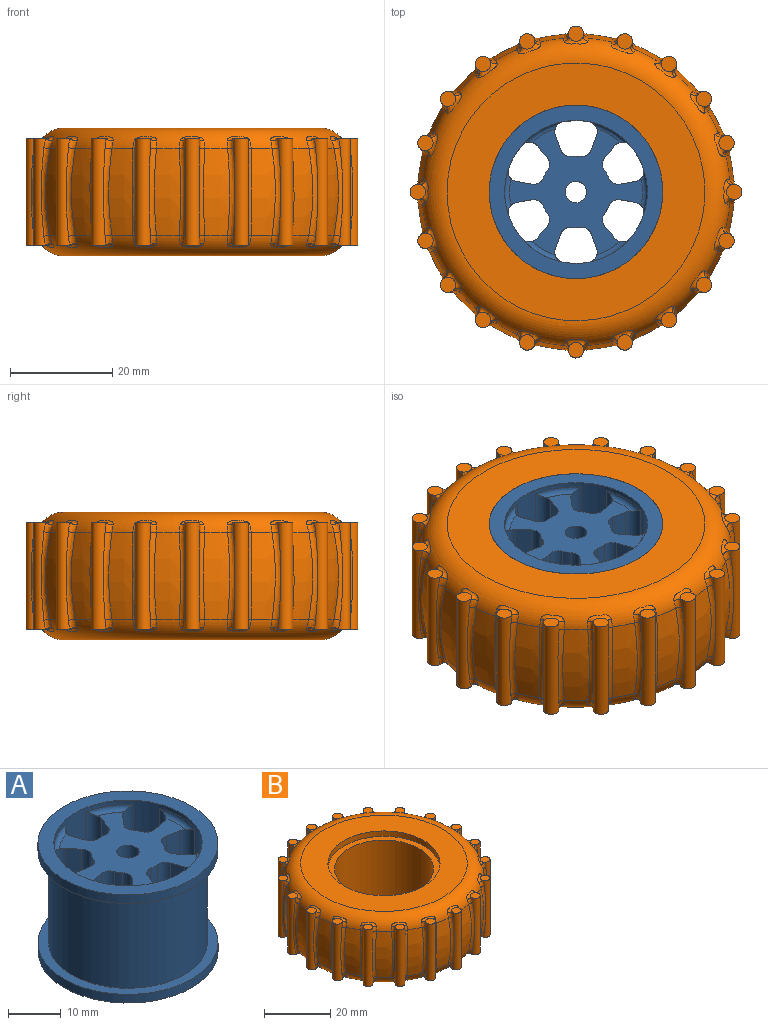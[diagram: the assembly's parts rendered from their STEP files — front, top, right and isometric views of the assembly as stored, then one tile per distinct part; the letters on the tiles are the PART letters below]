
ASSEMBLY  parts=2 mates=1
PART A: 60 faces, bbox 34x34x25 mm
  f0: cylinder r=15mm len=30mm, axis (0,0,-1), area 1979.2mm2, adj f19,f21
  f1: plane 16.45x3.01mm, normal (-0.17,0.98,0), area 49.3mm2, adj f3,f4,f13,f16
  f2: plane 16.45x2.34mm, normal (0.77,-0.64,0), area 49.3mm2, adj f5,f6,f13,f17
  f3: cylinder r=2mm len=20.5mm, axis (0,0,-1), area 62.2mm2, adj f1,f10,f13,f15,f16
  f4: cylinder r=2mm len=19.5mm, axis (0,0,-1), area 47.8mm2, adj f1,f8,f13,f16
  f5: cylinder r=2mm len=19.5mm, axis (0,0,-1), area 47.8mm2, adj f2,f8,f13,f17
  f6: cylinder r=2mm len=20.5mm, axis (0,0,-1), area 62.2mm2, adj f2,f10,f13,f14,f17
  f7: plane 34x34mm, normal (0,0,-1), area 292.2mm2, adj f10,f20
  f8: cylinder r=7mm len=23mm, axis (0,0,-1), area 358.6mm2, adj f4,f5,f12,f13,f16,f17,f25,f26
  f9: cylinder r=2.1mm len=23mm, axis (0,0,-1), area 303.5mm2, adj f12,f13
  f10: cylinder r=14mm len=28mm, axis (0,0,-1), area 1021.3mm2, adj f3,f6,f7,f11,f14,f15,f16,f17
  f11: plane 34x34mm, normal (0,0,1), area 292.2mm2, adj f10,f18
  f12: plane 14x14mm, normal (0,0,-1), area 140.1mm2, adj f8,f9
  f13: plane 26x24.68mm, normal (0,0,1), area 274.5mm2, adj f1,f2,f3,f4,f5,f6,f8,f9
  f14: torus R=13mm, axis (0,0,1), area 11.4mm2, adj f6,f10,f13,f24
  f15: torus R=13mm, axis (0,0,1), area 11.4mm2, adj f3,f10,f13,f59
  f16: torus R=10.5mm, axis (0,0,-1), area 52mm2, adj f1,f3,f4,f8,f10,f55,f58,f59
  f17: torus R=10.5mm, axis (0,0,-1), area 52mm2, adj f2,f5,f6,f8,f10,f22,f24,f25
  f18: cylinder r=17mm len=34mm, axis (0,0,1), area 213.6mm2, adj f11,f19
  f19: plane 34x34mm, normal (0,0,-1), area 201.1mm2, adj f0,f18
  f20: cylinder r=17mm len=34mm, axis (0,0,-1), area 213.6mm2, adj f7,f21
  f21: plane 34x34mm, normal (0,0,1), area 201.1mm2, adj f0,f20
  f22: plane 16.45x2.87mm, normal (-0.94,0.34,0), area 49.3mm2, adj f13,f17,f24,f25
  f23: plane 16.45x2.87mm, normal (0.94,0.34,0), area 49.3mm2, adj f13,f26,f27,f29
  f24: cylinder r=2mm len=20.5mm, axis (0,0,-1), area 62.2mm2, adj f10,f13,f14,f17,f22
  f25: cylinder r=2mm len=19.5mm, axis (0,0,-1), area 47.8mm2, adj f8,f13,f17,f22
  f26: cylinder r=2mm len=19.5mm, axis (0,0,-1), area 47.8mm2, adj f8,f13,f23,f29
  f27: cylinder r=2mm len=20.5mm, axis (0,0,-1), area 62.2mm2, adj f10,f13,f23,f28,f29
  f28: torus R=13mm, axis (0,0,1), area 11.4mm2, adj f10,f13,f27,f32
  f29: torus R=10.5mm, axis (0,0,-1), area 52mm2, adj f8,f10,f23,f26,f27,f30,f32,f33
  f30: plane 16.45x2.34mm, normal (-0.77,-0.64,0), area 49.3mm2, adj f13,f29,f32,f33
  f31: plane 16.45x3.01mm, normal (0.17,0.98,0), area 49.3mm2, adj f13,f34,f35,f37
  f32: cylinder r=2mm len=20.5mm, axis (0,0,-1), area 62.2mm2, adj f10,f13,f28,f29,f30
  f33: cylinder r=2mm len=19.5mm, axis (0,0,-1), area 47.8mm2, adj f8,f13,f29,f30
  f34: cylinder r=2mm len=19.5mm, axis (0,0,-1), area 47.8mm2, adj f8,f13,f31,f37
  f35: cylinder r=2mm len=20.5mm, axis (0,0,-1), area 62.2mm2, adj f10,f13,f31,f36,f37
  f36: torus R=13mm, axis (0,0,1), area 11.4mm2, adj f10,f13,f35,f40
  f37: torus R=10.5mm, axis (0,0,-1), area 52mm2, adj f8,f10,f31,f34,f35,f38,f40,f41
  f38: plane 16.45x3.01mm, normal (0.17,-0.98,0), area 49.3mm2, adj f13,f37,f40,f41
  f39: plane 16.45x2.34mm, normal (-0.77,0.64,0), area 49.3mm2, adj f13,f42,f43,f45
  f40: cylinder r=2mm len=20.5mm, axis (0,0,-1), area 62.2mm2, adj f10,f13,f36,f37,f38
  f41: cylinder r=2mm len=19.5mm, axis (0,0,-1), area 47.8mm2, adj f8,f13,f37,f38
  f42: cylinder r=2mm len=19.5mm, axis (0,0,-1), area 47.8mm2, adj f8,f13,f39,f45
  f43: cylinder r=2mm len=20.5mm, axis (0,0,-1), area 62.2mm2, adj f10,f13,f39,f44,f45
  f44: torus R=13mm, axis (0,0,1), area 11.4mm2, adj f10,f13,f43,f48
  f45: torus R=10.5mm, axis (0,0,-1), area 52mm2, adj f8,f10,f39,f42,f43,f46,f48,f49
  f46: plane 16.45x2.87mm, normal (0.94,-0.34,0), area 49.3mm2, adj f13,f45,f48,f49
  f47: plane 16.45x2.87mm, normal (-0.94,-0.34,0), area 49.3mm2, adj f13,f50,f51,f53
  f48: cylinder r=2mm len=20.5mm, axis (0,0,-1), area 62.2mm2, adj f10,f13,f44,f45,f46
  f49: cylinder r=2mm len=19.5mm, axis (0,0,-1), area 47.8mm2, adj f8,f13,f45,f46
  f50: cylinder r=2mm len=19.5mm, axis (0,0,-1), area 47.8mm2, adj f8,f13,f47,f53
  f51: cylinder r=2mm len=20.5mm, axis (0,0,-1), area 62.2mm2, adj f10,f13,f47,f52,f53
  f52: torus R=13mm, axis (0,0,1), area 11.4mm2, adj f10,f13,f51,f56
  f53: torus R=10.5mm, axis (0,0,-1), area 52mm2, adj f8,f10,f47,f50,f51,f54,f56,f57
  f54: plane 16.45x2.34mm, normal (0.77,0.64,0), area 49.3mm2, adj f13,f53,f56,f57
  f55: plane 16.45x3.01mm, normal (-0.17,-0.98,0), area 49.3mm2, adj f13,f16,f58,f59
  f56: cylinder r=2mm len=20.5mm, axis (0,0,-1), area 62.2mm2, adj f10,f13,f52,f53,f54
  f57: cylinder r=2mm len=19.5mm, axis (0,0,-1), area 47.8mm2, adj f8,f13,f53,f54
  f58: cylinder r=2mm len=19.5mm, axis (0,0,-1), area 47.8mm2, adj f8,f13,f16,f55
  f59: cylinder r=2mm len=20.5mm, axis (0,0,-1), area 62.2mm2, adj f10,f13,f15,f16,f55
PART B: 277 faces, bbox 65.5x65.5x25 mm
  f0: torus R=25.25mm, axis (0,0,-1), area 977.2mm2, adj f1,f2,f3,f4,f5,f6,f7,f8
  f1: revolved ~16.97x4.97mm, area 85.1mm2, adj f0,f21,f47,f246
  f2: revolved ~16.97x5.22mm, area 85.1mm2, adj f0,f21,f37,f243
  f3: revolved ~16.97x5.22mm, area 85.1mm2, adj f0,f21,f34,f234
  f4: revolved ~16.97x4.97mm, area 85.1mm2, adj f0,f21,f223,f233
  f5: revolved ~16.97x4.24mm, area 85.1mm2, adj f0,f21,f212,f222
  f6: revolved ~16.97x4.97mm, area 85.1mm2, adj f0,f21,f201,f211
  f7: revolved ~16.97x5.22mm, area 85.1mm2, adj f0,f21,f190,f200
  f8: revolved ~16.97x5.22mm, area 85.1mm2, adj f0,f21,f179,f189
  f9: revolved ~16.97x4.97mm, area 85.1mm2, adj f0,f21,f168,f178
  f10: revolved ~16.97x4.24mm, area 85.1mm2, adj f0,f21,f157,f167
  f11: revolved ~16.97x4.97mm, area 85.1mm2, adj f0,f21,f146,f156
  f12: revolved ~16.97x5.22mm, area 85.1mm2, adj f0,f21,f135,f145
  f13: revolved ~16.97x5.22mm, area 85.1mm2, adj f0,f21,f124,f134
  f14: revolved ~16.97x4.97mm, area 85.1mm2, adj f0,f21,f113,f123
  f15: revolved ~16.97x4.24mm, area 85.1mm2, adj f0,f21,f102,f112
  f16: revolved ~16.97x4.97mm, area 85.1mm2, adj f0,f21,f91,f101
  f17: revolved ~16.97x5.22mm, area 85.1mm2, adj f0,f21,f80,f90
  f18: revolved ~16.97x5.22mm, area 85.1mm2, adj f0,f21,f69,f79
  f19: revolved ~16.97x4.97mm, area 85.1mm2, adj f0,f21,f58,f68
  f20: revolved ~16.97x4.24mm, area 85.1mm2, adj f0,f21,f46,f57
  f21: torus R=25.25mm, axis (0,0,-1), area 977.2mm2, adj f1,f2,f3,f4,f5,f6,f7,f8
  f22: plane 34x34mm, normal (0,0,1), area 201.1mm2, adj f23,f28
  f23: cylinder r=15mm len=30mm, axis (0,0,-1), area 1979.2mm2, adj f22,f24
  f24: plane 34x34mm, normal (0,0,-1), area 201.1mm2, adj f23,f25
  f25: cylinder r=17mm len=34mm, axis (0,0,-1), area 213.6mm2, adj f24,f26
  f26: plane 50.51x50.51mm, normal (0,0,-1), area 1095.4mm2, adj f0,f25
  f27: plane 50.51x50.51mm, normal (0,0,1), area 1095.4mm2, adj f21,f28
  f28: cylinder r=17mm len=34mm, axis (0,0,-1), area 213.6mm2, adj f22,f27
  f29: cylinder r=1.5mm len=21mm, axis (0,0,1), area 87.2mm2, adj f30,f31,f32,f34,f35,f36,f37,f39
  f30: plane 3x3mm, normal (0,0,-1), area 7.1mm2, adj f29,f38
  f31: plane 3x3mm, normal (0,0,1), area 7.1mm2, adj f29,f33
  f32: bspline ~3.55x1.81mm, area 2.7mm2, adj f21,f29,f33,f34
  f33: bspline ~4.71x1.7mm, area 4.2mm2, adj f21,f31,f32,f35
  f34: bspline ~20.64x1.85mm, area 21.4mm2, adj f3,f29,f32,f36
  f35: bspline ~2.49x1.66mm, area 2.7mm2, adj f21,f29,f33,f37
  f36: bspline ~2.49x1.66mm, area 2.7mm2, adj f0,f29,f34,f38
  f37: bspline ~20.64x1.85mm, area 21.4mm2, adj f2,f29,f35,f39
  f38: bspline ~4.71x1.7mm, area 4.2mm2, adj f0,f30,f36,f39
  f39: bspline ~2.69x1.78mm, area 2.7mm2, adj f0,f29,f37,f38
  f40: plane 3x3mm, normal (0,0,-1), area 7.1mm2, adj f42,f49
  f41: plane 3x3mm, normal (0,0,1), area 7.1mm2, adj f42,f44
  f42: cylinder r=1.5mm len=21mm, axis (0,0,1), area 87.2mm2, adj f40,f41,f43,f45,f46,f47,f48,f50
  f43: bspline ~3.55x1.69mm, area 2.7mm2, adj f21,f42,f44,f47
  f44: bspline ~3.89x3.26mm, area 4.3mm2, adj f21,f41,f43,f45
  f45: bspline ~2.49x1.83mm, area 2.7mm2, adj f21,f42,f44,f46
  f46: bspline ~20.64x2.09mm, area 21.4mm2, adj f20,f42,f45,f48
  f47: bspline ~20.64x1.9mm, area 21.4mm2, adj f1,f42,f43,f50
  f48: bspline ~3.55x1.92mm, area 2.7mm2, adj f0,f42,f46,f49
  f49: bspline ~3.86x3.32mm, area 4.3mm2, adj f0,f40,f48,f50
  f50: bspline ~2.49x1.64mm, area 2.7mm2, adj f0,f42,f47,f49
  f51: plane 3x3mm, normal (0,0,-1), area 7.1mm2, adj f53,f60
  f52: plane 3x3mm, normal (0,0,1), area 7.1mm2, adj f53,f55
  f53: cylinder r=1.5mm len=21mm, axis (0,0,1), area 87.2mm2, adj f51,f52,f54,f56,f57,f58,f59,f61
  f54: bspline ~3.55x1.92mm, area 2.7mm2, adj f21,f53,f55,f57
  f55: bspline ~3.86x3.32mm, area 4.3mm2, adj f21,f52,f54,f56
  f56: bspline ~2.49x1.64mm, area 2.7mm2, adj f21,f53,f55,f58
  f57: bspline ~20.64x2.09mm, area 21.4mm2, adj f20,f53,f54,f61
  f58: bspline ~20.64x1.9mm, area 21.4mm2, adj f19,f53,f56,f59
  f59: bspline ~2.69x1.67mm, area 2.7mm2, adj f0,f53,f58,f60
  f60: bspline ~3.89x3.26mm, area 4.3mm2, adj f0,f51,f59,f61
  f61: bspline ~2.49x1.83mm, area 2.7mm2, adj f0,f53,f57,f60
  f62: plane 3x3mm, normal (0,0,-1), area 7.1mm2, adj f64,f71
  f63: plane 3x3mm, normal (0,0,1), area 7.1mm2, adj f64,f66
  f64: cylinder r=1.5mm len=21mm, axis (0,0,1), area 87.2mm2, adj f62,f63,f65,f67,f68,f69,f70,f72
  f65: bspline ~3.55x1.96mm, area 2.7mm2, adj f21,f64,f66,f68
  f66: bspline ~4.5x2.55mm, area 4.2mm2, adj f21,f63,f65,f67
  f67: bspline ~3.35x1.56mm, area 2.7mm2, adj f21,f64,f66,f69
  f68: bspline ~20.64x2.07mm, area 21.4mm2, adj f19,f64,f65,f72
  f69: bspline ~20.64x1.68mm, area 21.4mm2, adj f18,f64,f67,f70
  f70: bspline ~3.55x1.66mm, area 2.7mm2, adj f0,f64,f69,f71
  f71: bspline ~4.5x2.5mm, area 4.2mm2, adj f0,f62,f70,f72
  f72: bspline ~2.49x1.84mm, area 2.7mm2, adj f0,f64,f68,f71
  f73: plane 3x3mm, normal (0,0,-1), area 7.1mm2, adj f75,f82
  f74: plane 3x3mm, normal (0,0,1), area 7.1mm2, adj f75,f77
  f75: cylinder r=1.5mm len=21mm, axis (0,0,1), area 87.2mm2, adj f73,f74,f76,f78,f79,f80,f81,f83
  f76: bspline ~3.55x1.81mm, area 2.7mm2, adj f21,f75,f77,f79
  f77: bspline ~4.71x1.7mm, area 4.2mm2, adj f21,f74,f76,f78
  f78: bspline ~2.49x1.66mm, area 2.7mm2, adj f21,f75,f77,f80
  f79: bspline ~20.64x1.85mm, area 21.4mm2, adj f18,f75,f76,f83
  f80: bspline ~20.64x1.85mm, area 21.4mm2, adj f17,f75,f78,f81
  f81: bspline ~2.69x1.78mm, area 2.7mm2, adj f0,f75,f80,f82
  f82: bspline ~4.71x1.7mm, area 4.2mm2, adj f0,f73,f81,f83
  f83: bspline ~2.49x1.66mm, area 2.7mm2, adj f0,f75,f79,f82
  f84: plane 3x3mm, normal (0,0,-1), area 7.1mm2, adj f86,f93
  f85: plane 3x3mm, normal (0,0,1), area 7.1mm2, adj f86,f88
  f86: cylinder r=1.5mm len=21mm, axis (0,0,1), area 87.2mm2, adj f84,f85,f87,f89,f90,f91,f92,f94
  f87: bspline ~2.69x1.63mm, area 2.7mm2, adj f21,f86,f88,f90
  f88: bspline ~4.5x2.5mm, area 4.2mm2, adj f21,f85,f87,f89
  f89: bspline ~3.35x1.87mm, area 2.7mm2, adj f21,f86,f88,f91
  f90: bspline ~20.64x1.68mm, area 21.4mm2, adj f17,f86,f87,f94
  f91: bspline ~20.64x2.07mm, area 21.4mm2, adj f16,f86,f89,f92
  f92: bspline ~2.69x1.93mm, area 2.7mm2, adj f0,f86,f91,f93
  f93: bspline ~4.5x2.55mm, area 4.2mm2, adj f0,f84,f92,f94
  f94: bspline ~3.35x1.56mm, area 2.7mm2, adj f0,f86,f90,f93
  f95: plane 3x3mm, normal (0,0,-1), area 7.1mm2, adj f97,f104
  f96: plane 3x3mm, normal (0,0,1), area 7.1mm2, adj f97,f99
  f97: cylinder r=1.5mm len=21mm, axis (0,0,1), area 87.2mm2, adj f95,f96,f98,f100,f101,f102,f103,f105
  f98: bspline ~3.55x1.69mm, area 2.7mm2, adj f21,f97,f99,f101
  f99: bspline ~3.89x3.26mm, area 4.3mm2, adj f21,f96,f98,f100
  f100: bspline ~2.49x1.83mm, area 2.7mm2, adj f21,f97,f99,f102
  f101: bspline ~20.64x1.9mm, area 21.4mm2, adj f16,f97,f98,f105
  f102: bspline ~20.64x2.09mm, area 21.4mm2, adj f15,f97,f100,f103
  f103: bspline ~3.55x1.92mm, area 2.7mm2, adj f0,f97,f102,f104
  f104: bspline ~3.86x3.32mm, area 4.3mm2, adj f0,f95,f103,f105
  f105: bspline ~3.35x1.66mm, area 2.7mm2, adj f0,f97,f101,f104
  f106: plane 3x3mm, normal (0,0,-1), area 7.1mm2, adj f108,f115
  f107: plane 3x3mm, normal (0,0,1), area 7.1mm2, adj f108,f110
  f108: cylinder r=1.5mm len=21mm, axis (0,0,1), area 87.2mm2, adj f106,f107,f109,f111,f112,f113,f114,f116
  f109: bspline ~3.55x1.92mm, area 2.7mm2, adj f21,f108,f110,f112
  f110: bspline ~3.86x3.32mm, area 4.3mm2, adj f21,f107,f109,f111
  f111: bspline ~2.49x1.64mm, area 2.7mm2, adj f21,f108,f110,f113
  f112: bspline ~20.64x2.09mm, area 21.4mm2, adj f15,f108,f109,f116
  f113: bspline ~20.64x1.9mm, area 21.4mm2, adj f14,f108,f111,f114
  f114: bspline ~2.69x1.67mm, area 2.7mm2, adj f0,f108,f113,f115
  f115: bspline ~3.89x3.26mm, area 4.3mm2, adj f0,f106,f114,f116
  f116: bspline ~2.49x1.83mm, area 2.7mm2, adj f0,f108,f112,f115
  f117: plane 3x3mm, normal (0,0,-1), area 7.1mm2, adj f119,f126
  f118: plane 3x3mm, normal (0,0,1), area 7.1mm2, adj f119,f121
  f119: cylinder r=1.5mm len=21mm, axis (0,0,1), area 87.2mm2, adj f117,f118,f120,f122,f123,f124,f125,f127
  f120: bspline ~3.55x1.96mm, area 2.7mm2, adj f21,f119,f121,f123
  f121: bspline ~4.5x2.55mm, area 4.2mm2, adj f21,f118,f120,f122
  f122: bspline ~3.35x1.56mm, area 2.7mm2, adj f21,f119,f121,f124
  f123: bspline ~20.64x2.07mm, area 21.4mm2, adj f14,f119,f120,f127
  f124: bspline ~20.64x1.68mm, area 21.4mm2, adj f13,f119,f122,f125
  f125: bspline ~3.55x1.66mm, area 2.7mm2, adj f0,f119,f124,f126
  f126: bspline ~4.5x2.5mm, area 4.2mm2, adj f0,f117,f125,f127
  f127: bspline ~2.49x1.84mm, area 2.7mm2, adj f0,f119,f123,f126
  f128: plane 3x3mm, normal (0,0,-1), area 7.1mm2, adj f130,f137
  f129: plane 3x3mm, normal (0,0,1), area 7.1mm2, adj f130,f132
  f130: cylinder r=1.5mm len=21mm, axis (0,0,1), area 87.2mm2, adj f128,f129,f131,f133,f134,f135,f136,f138
  f131: bspline ~3.55x1.81mm, area 2.7mm2, adj f21,f130,f132,f134
  f132: bspline ~4.71x1.7mm, area 4.2mm2, adj f21,f129,f131,f133
  f133: bspline ~2.49x1.66mm, area 2.7mm2, adj f21,f130,f132,f135
  f134: bspline ~20.64x1.85mm, area 21.4mm2, adj f13,f130,f131,f138
  f135: bspline ~20.64x1.85mm, area 21.4mm2, adj f12,f130,f133,f136
  f136: bspline ~2.69x1.78mm, area 2.7mm2, adj f0,f130,f135,f137
  f137: bspline ~4.71x1.7mm, area 4.2mm2, adj f0,f128,f136,f138
  f138: bspline ~2.49x1.66mm, area 2.7mm2, adj f0,f130,f134,f137
  f139: plane 3x3mm, normal (0,0,-1), area 7.1mm2, adj f141,f148
  f140: plane 3x3mm, normal (0,0,1), area 7.1mm2, adj f141,f143
  f141: cylinder r=1.5mm len=21mm, axis (0,0,1), area 87.2mm2, adj f139,f140,f142,f144,f145,f146,f147,f149
  f142: bspline ~2.69x1.63mm, area 2.7mm2, adj f21,f141,f143,f145
  f143: bspline ~4.5x2.5mm, area 4.2mm2, adj f21,f140,f142,f144
  f144: bspline ~3.35x1.87mm, area 2.7mm2, adj f21,f141,f143,f146
  f145: bspline ~20.64x1.68mm, area 21.4mm2, adj f12,f141,f142,f149
  f146: bspline ~20.64x2.07mm, area 21.4mm2, adj f11,f141,f144,f147
  f147: bspline ~2.69x1.93mm, area 2.7mm2, adj f0,f141,f146,f148
  f148: bspline ~4.5x2.55mm, area 4.2mm2, adj f0,f139,f147,f149
  f149: bspline ~3.35x1.56mm, area 2.7mm2, adj f0,f141,f145,f148
  f150: plane 3x3mm, normal (0,0,-1), area 7.1mm2, adj f152,f159
  f151: plane 3x3mm, normal (0,0,1), area 7.1mm2, adj f152,f154
  f152: cylinder r=1.5mm len=21mm, axis (0,0,1), area 87.2mm2, adj f150,f151,f153,f155,f156,f157,f158,f160
  f153: bspline ~3.55x1.69mm, area 2.7mm2, adj f21,f152,f154,f156
  f154: bspline ~3.89x3.26mm, area 4.3mm2, adj f21,f151,f153,f155
  f155: bspline ~2.49x1.83mm, area 2.7mm2, adj f21,f152,f154,f157
  f156: bspline ~20.64x1.9mm, area 21.4mm2, adj f11,f152,f153,f160
  f157: bspline ~20.64x2.09mm, area 21.4mm2, adj f10,f152,f155,f158
  f158: bspline ~3.55x1.92mm, area 2.7mm2, adj f0,f152,f157,f159
  f159: bspline ~3.86x3.32mm, area 4.3mm2, adj f0,f150,f158,f160
  f160: bspline ~3.35x1.66mm, area 2.7mm2, adj f0,f152,f156,f159
  f161: plane 3x3mm, normal (0,0,-1), area 7.1mm2, adj f163,f170
  f162: plane 3x3mm, normal (0,0,1), area 7.1mm2, adj f163,f165
  f163: cylinder r=1.5mm len=21mm, axis (0,0,1), area 87.2mm2, adj f161,f162,f164,f166,f167,f168,f169,f171
  f164: bspline ~3.55x1.92mm, area 2.7mm2, adj f21,f163,f165,f167
  f165: bspline ~3.86x3.32mm, area 4.3mm2, adj f21,f162,f164,f166
  f166: bspline ~3.35x1.66mm, area 2.7mm2, adj f21,f163,f165,f168
  f167: bspline ~20.64x2.09mm, area 21.4mm2, adj f10,f163,f164,f171
  f168: bspline ~20.64x1.9mm, area 21.4mm2, adj f9,f163,f166,f169
  f169: bspline ~2.69x1.67mm, area 2.7mm2, adj f0,f163,f168,f170
  f170: bspline ~3.89x3.26mm, area 4.3mm2, adj f0,f161,f169,f171
  f171: bspline ~2.49x1.83mm, area 2.7mm2, adj f0,f163,f167,f170
  f172: plane 3x3mm, normal (0,0,-1), area 7.1mm2, adj f174,f181
  f173: plane 3x3mm, normal (0,0,1), area 7.1mm2, adj f174,f176
  f174: cylinder r=1.5mm len=21mm, axis (0,0,1), area 87.2mm2, adj f172,f173,f175,f177,f178,f179,f180,f182
  f175: bspline ~3.55x1.96mm, area 2.7mm2, adj f21,f174,f176,f178
  f176: bspline ~4.5x2.55mm, area 4.2mm2, adj f21,f173,f175,f177
  f177: bspline ~3.35x1.56mm, area 2.7mm2, adj f21,f174,f176,f179
  f178: bspline ~20.64x2.07mm, area 21.4mm2, adj f9,f174,f175,f182
  f179: bspline ~20.64x1.68mm, area 21.4mm2, adj f8,f174,f177,f180
  f180: bspline ~3.55x1.66mm, area 2.7mm2, adj f0,f174,f179,f181
  f181: bspline ~4.5x2.5mm, area 4.2mm2, adj f0,f172,f180,f182
  f182: bspline ~2.49x1.84mm, area 2.7mm2, adj f0,f174,f178,f181
  f183: plane 3x3mm, normal (0,0,-1), area 7.1mm2, adj f185,f192
  f184: plane 3x3mm, normal (0,0,1), area 7.1mm2, adj f185,f187
  f185: cylinder r=1.5mm len=21mm, axis (0,0,1), area 87.2mm2, adj f183,f184,f186,f188,f189,f190,f191,f193
  f186: bspline ~3.55x1.81mm, area 2.7mm2, adj f21,f185,f187,f189
  f187: bspline ~4.71x1.7mm, area 4.2mm2, adj f21,f184,f186,f188
  f188: bspline ~2.49x1.66mm, area 2.7mm2, adj f21,f185,f187,f190
  f189: bspline ~20.64x1.85mm, area 21.4mm2, adj f8,f185,f186,f193
  f190: bspline ~20.64x1.85mm, area 21.4mm2, adj f7,f185,f188,f191
  f191: bspline ~2.69x1.78mm, area 2.7mm2, adj f0,f185,f190,f192
  f192: bspline ~4.71x1.7mm, area 4.2mm2, adj f0,f183,f191,f193
  f193: bspline ~2.49x1.66mm, area 2.7mm2, adj f0,f185,f189,f192
  f194: plane 3x3mm, normal (0,0,-1), area 7.1mm2, adj f196,f203
  f195: plane 3x3mm, normal (0,0,1), area 7.1mm2, adj f196,f198
  f196: cylinder r=1.5mm len=21mm, axis (0,0,1), area 87.2mm2, adj f194,f195,f197,f199,f200,f201,f202,f204
  f197: bspline ~2.69x1.63mm, area 2.7mm2, adj f21,f196,f198,f200
  f198: bspline ~4.5x2.5mm, area 4.2mm2, adj f21,f195,f197,f199
  f199: bspline ~3.35x1.87mm, area 2.7mm2, adj f21,f196,f198,f201
  f200: bspline ~20.64x1.68mm, area 21.4mm2, adj f7,f196,f197,f204
  f201: bspline ~20.64x2.07mm, area 21.4mm2, adj f6,f196,f199,f202
  f202: bspline ~2.69x1.93mm, area 2.7mm2, adj f0,f196,f201,f203
  f203: bspline ~4.5x2.55mm, area 4.2mm2, adj f0,f194,f202,f204
  f204: bspline ~3.35x1.56mm, area 2.7mm2, adj f0,f196,f200,f203
  f205: plane 3x3mm, normal (0,0,-1), area 7.1mm2, adj f207,f214
  f206: plane 3x3mm, normal (0,0,1), area 7.1mm2, adj f207,f209
  f207: cylinder r=1.5mm len=21mm, axis (0,0,1), area 87.2mm2, adj f205,f206,f208,f210,f211,f212,f213,f215
  f208: bspline ~3.55x1.69mm, area 2.7mm2, adj f21,f207,f209,f211
  f209: bspline ~3.89x3.26mm, area 4.3mm2, adj f21,f206,f208,f210
  f210: bspline ~2.49x1.83mm, area 2.7mm2, adj f21,f207,f209,f212
  f211: bspline ~20.64x1.9mm, area 21.4mm2, adj f6,f207,f208,f215
  f212: bspline ~20.64x2.09mm, area 21.4mm2, adj f5,f207,f210,f213
  f213: bspline ~3.55x1.92mm, area 2.7mm2, adj f0,f207,f212,f214
  f214: bspline ~3.86x3.32mm, area 4.3mm2, adj f0,f205,f213,f215
  f215: bspline ~2.49x1.64mm, area 2.7mm2, adj f0,f207,f211,f214
  f216: plane 3x3mm, normal (0,0,-1), area 7.1mm2, adj f218,f225
  f217: plane 3x3mm, normal (0,0,1), area 7.1mm2, adj f218,f220
  f218: cylinder r=1.5mm len=21mm, axis (0,0,1), area 87.2mm2, adj f216,f217,f219,f221,f222,f223,f224,f226
  f219: bspline ~3.55x1.92mm, area 2.7mm2, adj f21,f218,f220,f222
  f220: bspline ~3.86x3.32mm, area 4.3mm2, adj f21,f217,f219,f221
  f221: bspline ~3.35x1.66mm, area 2.7mm2, adj f21,f218,f220,f223
  f222: bspline ~20.64x2.09mm, area 21.4mm2, adj f5,f218,f219,f226
  f223: bspline ~20.64x1.9mm, area 21.4mm2, adj f4,f218,f221,f224
  f224: bspline ~2.69x1.67mm, area 2.7mm2, adj f0,f218,f223,f225
  f225: bspline ~3.89x3.26mm, area 4.3mm2, adj f0,f216,f224,f226
  f226: bspline ~2.49x1.83mm, area 2.7mm2, adj f0,f218,f222,f225
  f227: plane 3x3mm, normal (0,0,-1), area 7.1mm2, adj f229,f236
  f228: plane 3x3mm, normal (0,0,1), area 7.1mm2, adj f229,f231
  f229: cylinder r=1.5mm len=21mm, axis (0,0,1), area 87.2mm2, adj f227,f228,f230,f232,f233,f234,f235,f237
  f230: bspline ~3.55x1.96mm, area 2.7mm2, adj f21,f229,f231,f233
  f231: bspline ~4.5x2.55mm, area 4.2mm2, adj f21,f228,f230,f232
  f232: bspline ~3.35x1.56mm, area 2.7mm2, adj f21,f229,f231,f234
  f233: bspline ~20.64x2.07mm, area 21.4mm2, adj f4,f229,f230,f237
  f234: bspline ~20.64x1.68mm, area 21.4mm2, adj f3,f229,f232,f235
  f235: bspline ~3.55x1.66mm, area 2.7mm2, adj f0,f229,f234,f236
  f236: bspline ~4.5x2.5mm, area 4.2mm2, adj f0,f227,f235,f237
  f237: bspline ~2.49x1.84mm, area 2.7mm2, adj f0,f229,f233,f236
  f238: cylinder r=1.5mm len=21mm, axis (0,0,1), area 87.2mm2, adj f239,f240,f241,f243,f244,f245,f246,f248
  f239: plane 3x3mm, normal (0,0,-1), area 7.1mm2, adj f238,f247
  f240: plane 3x3mm, normal (0,0,1), area 7.1mm2, adj f238,f242
  f241: bspline ~2.69x1.63mm, area 2.7mm2, adj f21,f238,f242,f243
  f242: bspline ~4.5x2.5mm, area 4.2mm2, adj f21,f240,f241,f244
  f243: bspline ~20.64x1.68mm, area 21.4mm2, adj f2,f238,f241,f245
  f244: bspline ~3.35x1.87mm, area 2.7mm2, adj f21,f238,f242,f246
  f245: bspline ~3.35x1.56mm, area 2.7mm2, adj f0,f238,f243,f247
  f246: bspline ~20.64x2.07mm, area 21.4mm2, adj f1,f238,f244,f248
  f247: bspline ~4.5x2.55mm, area 4.2mm2, adj f0,f239,f245,f248
  f248: bspline ~2.69x1.93mm, area 2.7mm2, adj f0,f238,f246,f247
  f249: torus R=24.04mm, axis (0,0,-1), area 1180.7mm2, adj f250,f256
  f250: plane 48.08x48.08mm, normal (0,0,1), area 153.5mm2, adj f249,f251
  f251: torus R=23mm, axis (0,0,-1), area 977.9mm2, adj f250,f252
  f252: cylinder r=18mm len=36mm, axis (0,0,-1), area 1470.3mm2, adj f251,f253
  f253: torus R=23mm, axis (0,0,-1), area 977.9mm2, adj f252,f254
  f254: plane 48.08x48.08mm, normal (0,0,-1), area 153.5mm2, adj f253,f255
  f255: torus R=24.04mm, axis (0,0,-1), area 1180.7mm2, adj f254,f256
  f256: revolved ~59.24x59.24mm, area 2623.2mm2, adj f249,f255,f257,f258,f259,f260,f261,f262
  f257: cylinder r=1.5mm len=6.32mm, axis (0,0,1), area 5.7mm2, adj f256
  f258: cylinder r=1.5mm len=6.33mm, axis (0,0,1), area 5.9mm2, adj f256
  f259: cylinder r=1.5mm len=6.33mm, axis (0,0,1), area 5.9mm2, adj f256
  f260: cylinder r=1.5mm len=6.33mm, axis (0,0,1), area 5.9mm2, adj f256
  f261: cylinder r=1.5mm len=6.33mm, axis (0,0,1), area 5.9mm2, adj f256
  f262: cylinder r=1.5mm len=6.33mm, axis (0,0,1), area 5.9mm2, adj f256
  f263: cylinder r=1.5mm len=6.33mm, axis (0,0,1), area 5.9mm2, adj f256
  f264: cylinder r=1.5mm len=6.33mm, axis (0,0,1), area 5.9mm2, adj f256
  f265: cylinder r=1.5mm len=6.33mm, axis (0,0,1), area 5.9mm2, adj f256
  f266: cylinder r=1.5mm len=6.33mm, axis (0,0,1), area 5.9mm2, adj f256
  f267: cylinder r=1.5mm len=6.33mm, axis (0,0,1), area 5.9mm2, adj f256
  f268: cylinder r=1.5mm len=6.33mm, axis (0,0,1), area 5.9mm2, adj f256
  f269: cylinder r=1.5mm len=6.33mm, axis (0,0,1), area 5.9mm2, adj f256
  f270: cylinder r=1.5mm len=6.33mm, axis (0,0,1), area 5.9mm2, adj f256
  f271: cylinder r=1.5mm len=6.33mm, axis (0,0,1), area 5.9mm2, adj f256
  f272: cylinder r=1.5mm len=6.33mm, axis (0,0,1), area 5.9mm2, adj f256
  f273: cylinder r=1.5mm len=6.33mm, axis (0,0,1), area 5.9mm2, adj f256
  f274: cylinder r=1.5mm len=6.33mm, axis (0,0,1), area 5.9mm2, adj f256
  f275: cylinder r=1.5mm len=6.33mm, axis (0,0,1), area 5.9mm2, adj f256
  f276: cylinder r=1.5mm len=6.33mm, axis (0,0,1), area 5.9mm2, adj f256
PLACE A t=(0.59,2.04,-2.93)mm fixed
PLACE B t=(0.59,2.04,-2.93)mm
MATE fastened B.f0 <-> A.f9  axis (0,0,-1) through (0.59,2.04,20.07)mm
